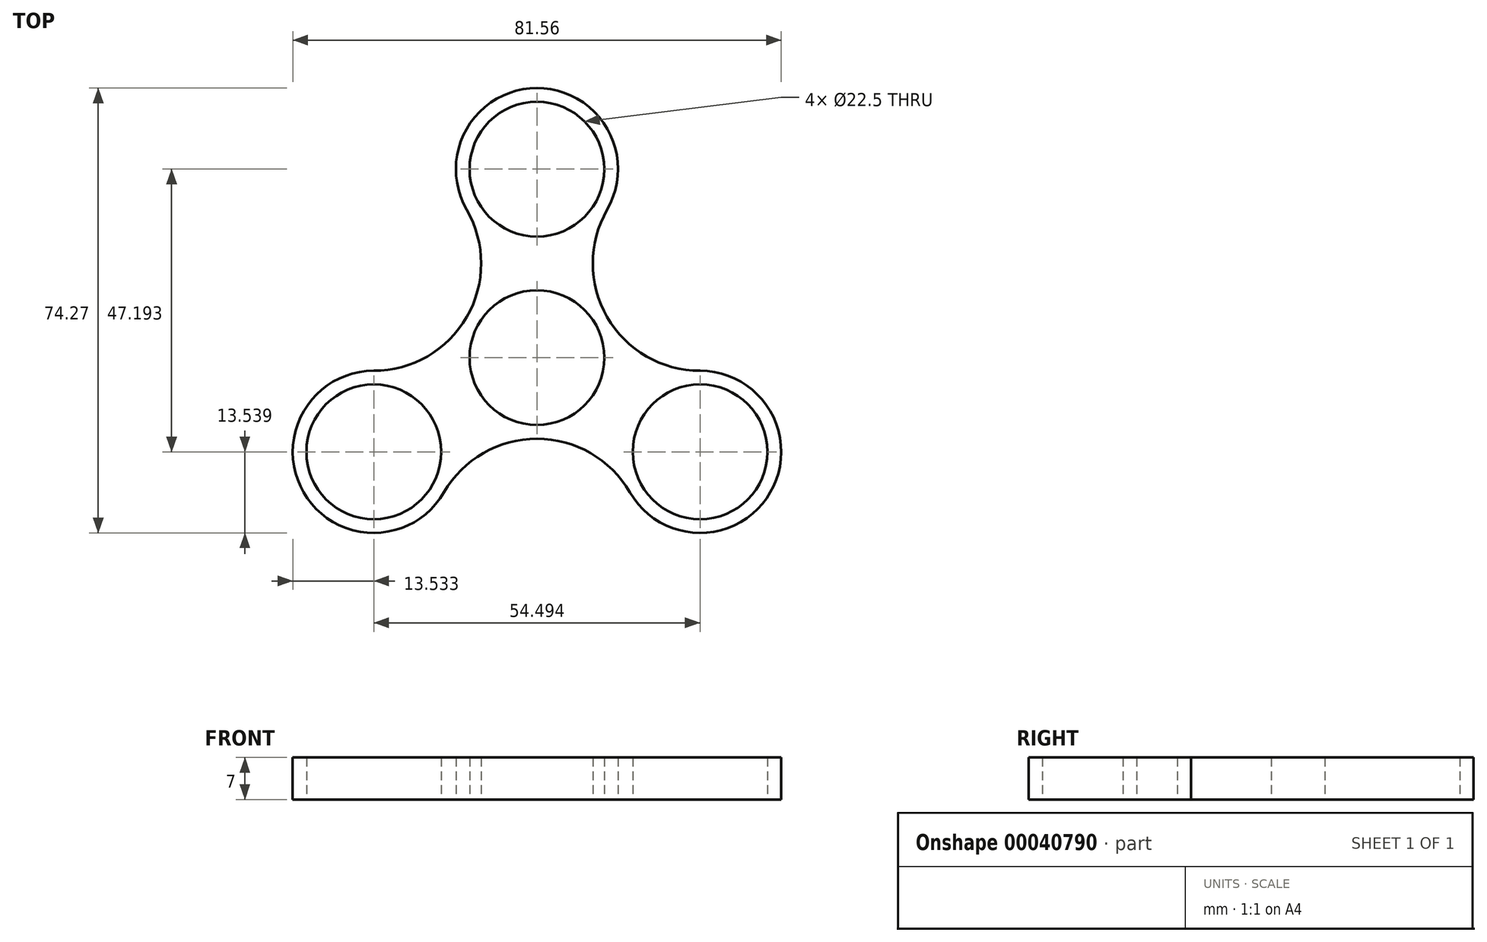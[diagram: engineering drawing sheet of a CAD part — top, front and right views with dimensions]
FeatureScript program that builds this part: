
annotation { "Feature Type Name" : "Feature", "Feature Type Description" : "" }
export const myFeature = defineFeature(function(context is Context, id is Id, definition is map)
    precondition{}
    {
        {
            var Q0;
            Q0=qCreatedBy(makeId("Top.planeOp"),FACE);
            var sketch = newSketch(context, id + "F0", { "sketchPlane" : qUnion([Q0])});
            skArc(sketch, "E0", {"start": v(11.72, 24.7) * mm, "mid": v(0, 45) * mm, "end": v(-11.72, 24.7) * mm});
            skPoint(sketch, "E1.center", {"position": v(0, 0) * mm});
            skCircle(sketch, "E2", {"center": v(0, 31.46) * mm, "radius": 11.25 * mm});
            skArc(sketch, "E3.1.4", {"start": v(-27.25, -2.2) * mm, "mid": v(-38.97, -22.5) * mm, "end": v(-15.52, -22.5) * mm});
            skCircle(sketch, "E3.1.5", {"center": v(-27.25, -15.73) * mm, "radius": 11.25 * mm});
            skArc(sketch, "E3.2.4", {"start": v(15.52, -22.5) * mm, "mid": v(38.97, -22.5) * mm, "end": v(27.25, -2.2) * mm});
            skCircle(sketch, "E3.2.5", {"center": v(27.25, -15.73) * mm, "radius": 11.25 * mm});
            skCircle(sketch, "E4", {"center": v(0, 0) * mm, "radius": 13.54 * mm});
            skPoint(sketch, "E5", {"position": v(0, -13.54) * mm});
            skArc(sketch, "E6", {"start": v(15.52, -22.5) * mm, "mid": v(0, -13.54) * mm, "end": v(-15.52, -22.5) * mm});
            skArc(sketch, "E7", {"start": v(-27.25, -2.2) * mm, "mid": v(-11.72, 6.77) * mm, "end": v(-11.72, 24.7) * mm});
            skArc(sketch, "E8", {"start": v(11.72, 24.7) * mm, "mid": v(11.72, 6.77) * mm, "end": v(27.25, -2.2) * mm});
            skCircle(sketch, "E9", {"center": v(0, 0) * mm, "radius": 11.25 * mm});
            skSolve(sketch);
        }
        {
            var Q0;
            {var subQ1=sQuery(id+"F0.wireOp",EDGE,"E0");Q0=makeQuery(id+"F0.imprint","IMPRINT",FACE,{"disambiguationData":[TD([[makeQuery(id+"F0.imprint","IMPRINT",EDGE,{"derivedFrom":subQ1}),1.0]])]});}
            var Q1;
            {var subQ1=sQuery(id+"F0.wireOp",EDGE,"E3.1.4");Q1=makeQuery(id+"F0.imprint","IMPRINT",FACE,{"disambiguationData":[TD([[makeQuery(id+"F0.imprint","IMPRINT",EDGE,{"derivedFrom":subQ1}),1.0]])]});}
            var Q2;
            Q2=makeQuery(id+"F0.imprint","IMPRINT",FACE,{"disambiguationData":[TD([[makeQuery(id+"F0.imprint","IMPRINT",EDGE,{"derivedFrom":sQuery(id+"F0.wireOp",EDGE,"E9")}),-1.0]])]});
            var Q3;
            {var subQ5=sQuery(id+"F0.wireOp",EDGE,"E3.2.4");Q3=makeQuery(id+"F0.imprint","IMPRINT",FACE,{"disambiguationData":[TD([[makeQuery(id+"F0.imprint","IMPRINT",EDGE,{"derivedFrom":subQ5}),1.0]])]});}
            extrude(context, id + "F1", {"entities" : qUnion([Q0, Q1, Q2, Q3]), "depth" : 7 * mm, "offsetDistance" : 25.4 * mm});
        }
    });
